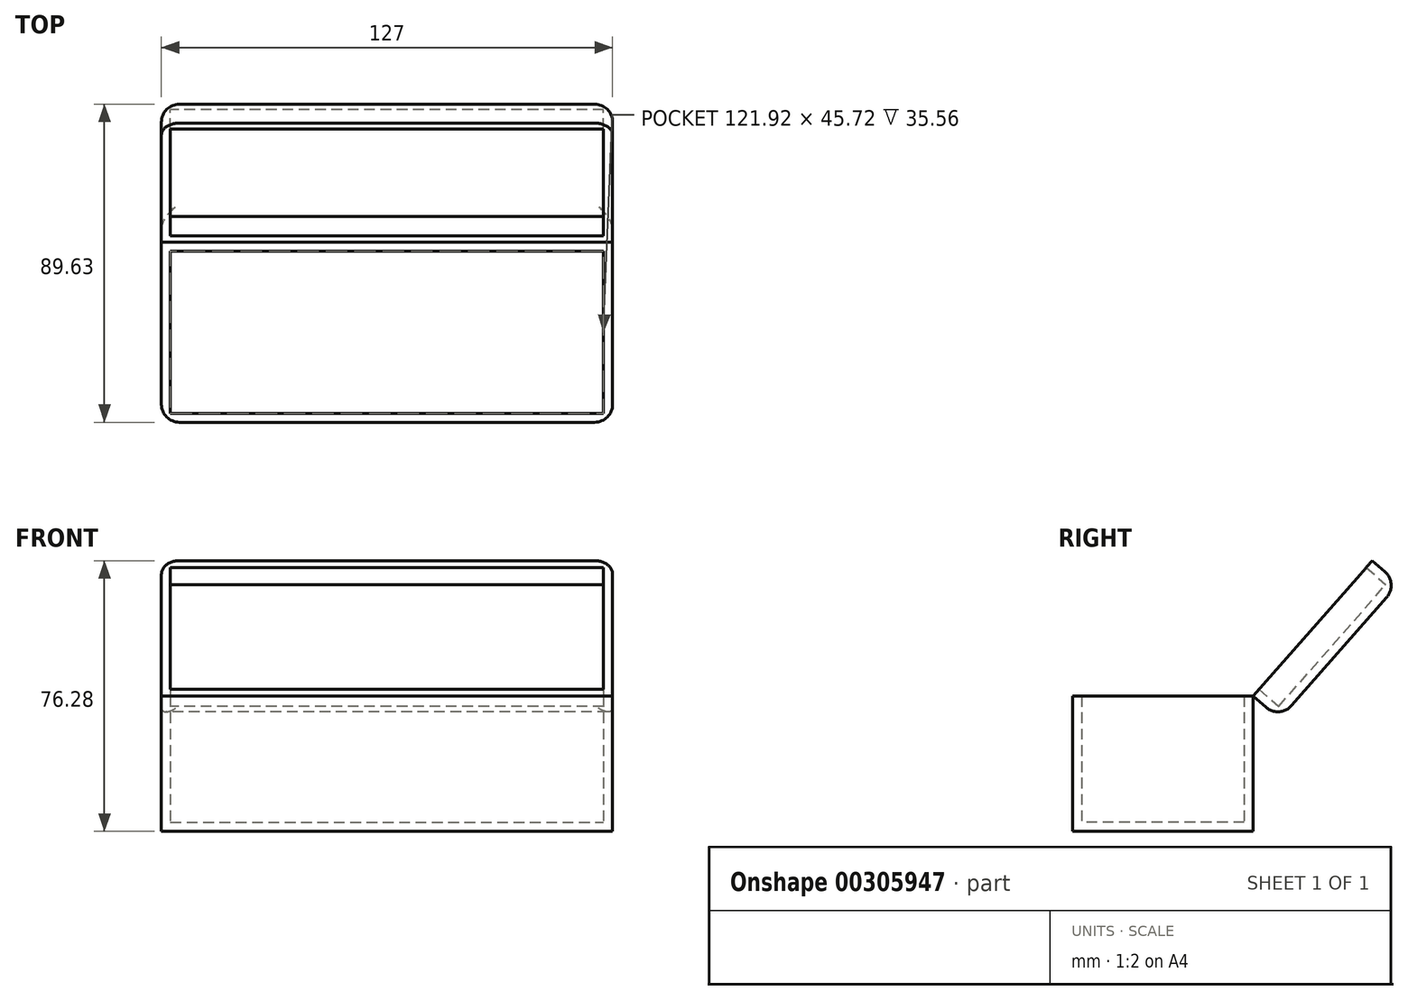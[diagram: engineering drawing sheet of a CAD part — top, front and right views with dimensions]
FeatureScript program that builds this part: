
annotation { "Feature Type Name" : "Feature", "Feature Type Description" : "" }
export const myFeature = defineFeature(function(context is Context, id is Id, definition is map)
    precondition{}
    {
        {
            var Q0;
            Q0=qCreatedBy(makeId("Top.planeOp"),FACE);
            var sketch = newSketch(context, id + "F0", { "sketchPlane" : qUnion([Q0])});
            skLineSegment(sketch, "E0.bottom", {"start": v(-76.2, 17.69) * mm, "end": v(50.8, 17.69) * mm});
            skLineSegment(sketch, "E0.top", {"start": v(-76.2, -33.11) * mm, "end": v(50.8, -33.11) * mm});
            skLineSegment(sketch, "E0.left", {"start": v(-76.2, 17.69) * mm, "end": v(-76.2, -33.11) * mm});
            skLineSegment(sketch, "E0.right", {"start": v(50.8, 17.69) * mm, "end": v(50.8, -33.11) * mm});
            skSolve(sketch);
        }
        {
            var Q0;
            Q0=makeQuery(id+"F0.imprint","IMPRINT",FACE,{"disambiguationData":[TD([[makeQuery(id+"F0.imprint","IMPRINT",EDGE,{"derivedFrom":sQuery(id+"F0.wireOp",EDGE,"E0.bottom")}),-1.0]])]});
            extrude(context, id + "F1", {"entities" : qUnion([Q0]), "depth" : 38.1 * mm});
        }
        {
            var Q0;
            Q0=makeQuery(id+"F1.opExtrude","CAP_FACE",FACE,{"disambiguationData":[OSD([sQuery(id+"F0.wireOp",EDGE,"E0.bottom"),sQuery(id+"F0.wireOp",EDGE,"E0.top"),sQuery(id+"F0.wireOp",EDGE,"E0.left"),sQuery(id+"F0.wireOp",EDGE,"E0.right")])],"isStart":false});
            var Q1;
            Q1=makeQuery(id+"F1.opExtrude","SWEPT_BODY",BODY,{"disambiguationData":[OSD([sQuery(id+"F0.wireOp",EDGE,"E0.bottom"),sQuery(id+"F0.wireOp",EDGE,"E0.top"),sQuery(id+"F0.wireOp",EDGE,"E0.left"),sQuery(id+"F0.wireOp",EDGE,"E0.right")])]});
            shell(context, id + "F2", {"entities" : qUnion([Q0]), "parts" : qUnion([Q1]), "thickness" : 2.54 * mm});
        }
        {
            var Q0;
            Q0=makeQuery(id+"F1.opExtrude","SWEPT_FACE",FACE,{"disambiguationData":[OSD([sQuery(id+"F0.wireOp",EDGE,"E0.left")])]});
            var sketch = newSketch(context, id + "F3", { "sketchPlane" : qUnion([Q0])});
            skLineSegment(sketch, "E1", {"start": v(-17.69, 38.1) * mm, "end": v(-51.2, 76.28) * mm});
            skLineSegment(sketch, "E2", {"start": v(-17.69, 38.1) * mm, "end": v(-25.1, 31.6) * mm});
            skLineSegment(sketch, "E3", {"start": v(-25.1, 31.6) * mm, "end": v(-58.62, 69.78) * mm});
            skLineSegment(sketch, "E4", {"start": v(-51.2, 76.28) * mm, "end": v(-58.62, 69.78) * mm});
            skSolve(sketch);
        }
        {
            var Q0;
            Q0=makeQuery(id+"F3.imprint","IMPRINT",FACE,{"disambiguationData":[TD([[makeQuery(id+"F3.imprint","IMPRINT",EDGE,{"derivedFrom":sQuery(id+"F3.wireOp",EDGE,"E1")}),1.0]])]});
            extrude(context, id + "F4", {"entities" : qUnion([Q0]), "oppositeDirection" : true, "depth" : 127 * mm});
        }
        {
            var Q0;
            Q0=makeQuery(id+"F4.opExtrude","SWEPT_FACE",FACE,{"disambiguationData":[OSD([sQuery(id+"F3.wireOp",EDGE,"E1")])]});
            shell(context, id + "F5", {"entities" : qUnion([Q0]), "thickness" : 2.54 * mm});
        }
        {
            var Q0;
            Q0=makeQuery(id+"F1.opExtrude","SWEPT_EDGE",EDGE,{"disambiguationData":[OSD([sQuery(id+"F0.wireOp",EDGE,"E0.top"),sQuery(id+"F0.wireOp",EDGE,"E0.left")])]});
            var Q1;
            Q1=makeQuery(id+"F1.opExtrude","SWEPT_EDGE",EDGE,{"disambiguationData":[OSD([sQuery(id+"F0.wireOp",EDGE,"E0.top"),sQuery(id+"F0.wireOp",EDGE,"E0.right")])]});
            var Q2;
            Q2=makeQuery(id+"F4.opExtrude","SWEPT_EDGE",EDGE,{"disambiguationData":[OSD([sQuery(id+"F3.wireOp",EDGE,"E3"),sQuery(id+"F3.wireOp",EDGE,"E4")])]});
            var Q3;
            Q3=makeQuery(id+"F4.opExtrude","CAP_EDGE",EDGE,{"disambiguationData":[OSD([sQuery(id+"F3.wireOp",EDGE,"E3")])],"isStart":false});
            var Q4;
            Q4=makeQuery(id+"F4.opExtrude","CAP_EDGE",EDGE,{"disambiguationData":[OSD([sQuery(id+"F3.wireOp",EDGE,"E4")])],"isStart":false});
            var Q5;
            Q5=makeQuery(id+"F4.opExtrude","CAP_EDGE",EDGE,{"disambiguationData":[OSD([sQuery(id+"F3.wireOp",EDGE,"E3")])],"isStart":true});
            var Q6;
            Q6=makeQuery(id+"F4.opExtrude","CAP_EDGE",EDGE,{"disambiguationData":[OSD([sQuery(id+"F3.wireOp",EDGE,"E4")])],"isStart":true});
            var Q7;
            Q7=makeQuery(id+"F4.opExtrude","SWEPT_EDGE",EDGE,{"disambiguationData":[OSD([sQuery(id+"F3.wireOp",EDGE,"E2"),sQuery(id+"F3.wireOp",EDGE,"E3")])]});
            fillet(context, id + "F6", {"entities" : qUnion([Q0, Q1, Q2, Q3, Q4, Q5, Q6, Q7]), "radius" : 5.08 * mm, "tangentPropagation" : true, "allowEdgeOverflow" : false});
        }
    });
